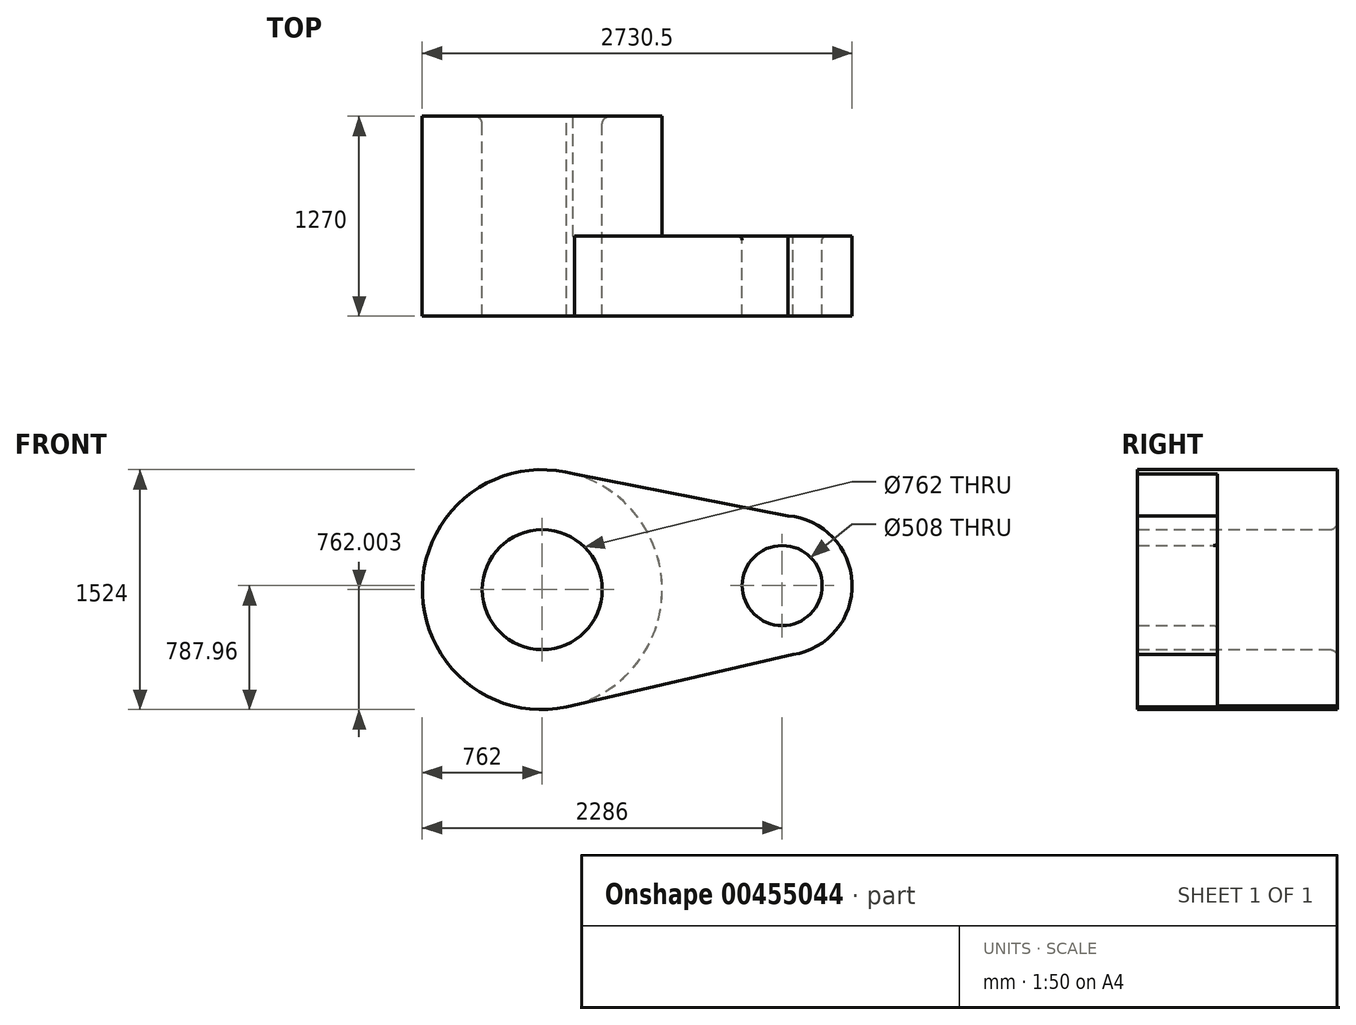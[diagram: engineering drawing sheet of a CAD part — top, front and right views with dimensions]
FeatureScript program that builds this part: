
annotation { "Feature Type Name" : "Feature", "Feature Type Description" : "" }
export const myFeature = defineFeature(function(context is Context, id is Id, definition is map)
    precondition{}
    {
        {
            var Q0;
            Q0=qCreatedBy(makeId("Front.planeOp"),FACE);
            var sketch = newSketch(context, id + "F0", { "sketchPlane" : qUnion([Q0])});
            skCircle(sketch, "E0", {"center": v(0, -25.96) * mm, "radius": 762 * mm});
            skCircle(sketch, "E1", {"center": v(1524, 0) * mm, "radius": 444.5 * mm});
            skLineSegment(sketch, "E2", {"start": v(203.7, 708.31) * mm, "end": v(1559.43, 443.09) * mm});
            skLineSegment(sketch, "E3", {"start": v(152.74, -772.5) * mm, "end": v(1592.73, -439.15) * mm});
            skCircle(sketch, "E4", {"center": v(0, -25.96) * mm, "radius": 381 * mm});
            skCircle(sketch, "E5", {"center": v(1524, 0) * mm, "radius": 254 * mm});
            skSolve(sketch);
        }
        {
            var Q0;
            Q0=makeQuery(id+"F0.imprint","IMPRINT",FACE,{"disambiguationData":[TD([[makeQuery(id+"F0.imprint","IMPRINT",EDGE,{"derivedFrom":sQuery(id+"F0.wireOp",EDGE,"E4")}),-1.0]])]});
            var Q1;
            {var subQ0=sQuery(id+"F0.wireOp",EDGE,"E2");Q1=makeQuery(id+"F0.imprint","IMPRINT",FACE,{"disambiguationData":[TD([[makeQuery(id+"F0.imprint","IMPRINT",EDGE,{"derivedFrom":subQ0}),-1.0]])]});}
            var Q2;
            Q2=makeQuery(id+"F0.imprint","IMPRINT",FACE,{"disambiguationData":[TD([[makeQuery(id+"F0.imprint","IMPRINT",EDGE,{"derivedFrom":sQuery(id+"F0.wireOp",EDGE,"E5")}),-1.0]])]});
            extrude(context, id + "F1", {"entities" : qUnion([Q0, Q1, Q2]), "depth" : 508 * mm});
        }
        {
            var Q0;
            Q0=makeQuery(id+"F0.imprint","IMPRINT",FACE,{"disambiguationData":[TD([[makeQuery(id+"F0.imprint","IMPRINT",EDGE,{"derivedFrom":sQuery(id+"F0.wireOp",EDGE,"E4")}),-1.0]])]});
            extrude(context, id + "F2", {"entities" : qUnion([Q0]), "operationType" : NewBodyOperationType.ADD, "oppositeDirection" : true, "depth" : 762 * mm});
        }
        {
            var Q0;
            Q0=makeQuery(id+"F2.opExtrude","CAP_EDGE",EDGE,{"disambiguationData":[OSD([sQuery(id+"F0.wireOp",EDGE,"E4")])],"isStart":false});
            fillet(context, id + "F3", {"entities" : qUnion([Q0]), "radius" : 50.8 * mm, "tangentPropagation" : true, "allowEdgeOverflow" : false});
        }
        {
            var Q0;
            Q0=makeQuery(id+"F1.opExtrude","CAP_EDGE",EDGE,{"disambiguationData":[OSD([sQuery(id+"F0.wireOp",EDGE,"E5")])],"isStart":true});
            fillet(context, id + "F4", {"entities" : qUnion([Q0]), "radius" : 25.4 * mm, "tangentPropagation" : true, "allowEdgeOverflow" : false});
        }
    });
